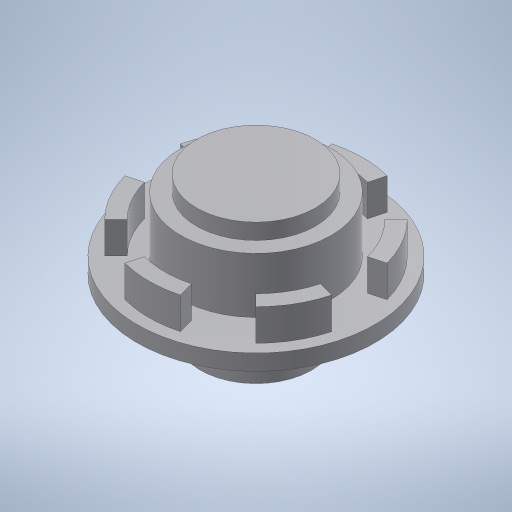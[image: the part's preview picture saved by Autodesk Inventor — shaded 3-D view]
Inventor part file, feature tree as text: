
AUTODESK INVENTOR PART (.ipt)
format: ipt  version: 2023.1 (Build 271208000, 208)  size: 293,376 bytes
history: native  units: mm
features: extrude x5, sketch x5, projected_geometry x3
ambient origin geometry x8: Origin, YZ Plane, XZ Plane, XY Plane, X Axis, Y Axis, Z Axis, Center Point
bodies: Solid1 (feature_tree)
feature tree (13):
  extrude  "Extrusion1"  Depth=2.0mm TaperAngle=0.0deg
  extrude  "Extrusion2"  Depth=4.0mm
  extrude  "Extrusion3"  Depth=15.0mm
  extrude  "Extrusion4"  Depth=2.0mm
  extrude  "Extrusion5"  [1 undecoded]
  sketch  "Sketch1"  dims[d0=30.0mm d1=2.0mm d2=0.0mm]
  sketch  "Sketch2"  dims[d10=4.0mm d11=0.0mm d12=19.0mm]
  projected_geometry  "Projected Loop1"
  sketch  "Sketch3"  dims[d13=7.0mm d14=0.0mm d15=15.0mm]
  projected_geometry  "Projected Loop2"
  sketch  "Sketch4"  dims[d16=2.0mm d17=0.0mm d18=14.0mm]
  projected_geometry  "Projected Loop3"
  sketch  "Sketch5"  dims[d19=7.0mm d20=0.0mm]
note: 1 required parameter value undecoded (feature->parameter linkage not recoverable at this tier; creation-order binding heuristic only, values carry confidence <= 0.55)
